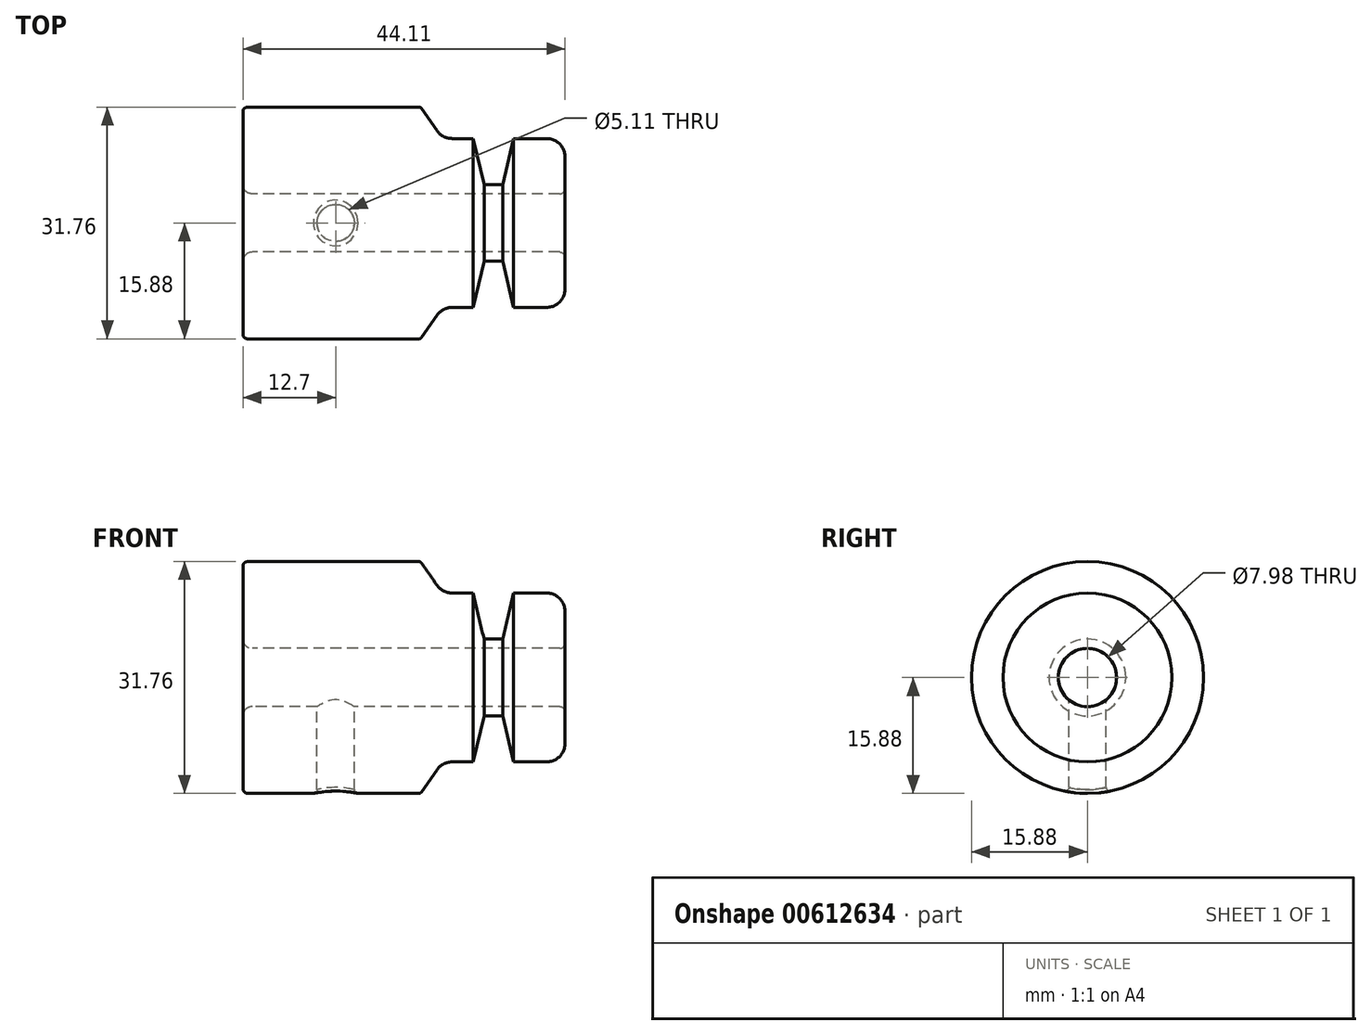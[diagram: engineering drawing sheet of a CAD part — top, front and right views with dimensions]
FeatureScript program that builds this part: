
annotation { "Feature Type Name" : "Feature", "Feature Type Description" : "" }
export const myFeature = defineFeature(function(context is Context, id is Id, definition is map)
    precondition{}
    {
        {
            var Q0;
            Q0=qCreatedBy(makeId("Top.planeOp"),FACE);
            var sketch = newSketch(context, id + "F0", { "sketchPlane" : qUnion([Q0])});
            skLineSegment(sketch, "E0", {"start": v(-39.61, 0) * mm, "end": v(40.88, 0) * mm});
            skLineSegment(sketch, "E1", {"start": v(-11.43, 3.99) * mm, "end": v(21.6, 3.99) * mm});
            skLineSegment(sketch, "E2", {"start": v(31.41, 11.27) * mm, "end": v(31.41, 11.57) * mm});
            skLineSegment(sketch, "E3", {"start": v(15.69, 15.88) * mm, "end": v(-12.07, 15.88) * mm});
            skPoint(sketch, "E4.startSnap0", {"position": v(-21.2, 9.35) * mm});
            skLineSegment(sketch, "E5", {"start": v(-12.7, 15.24) * mm, "end": v(-12.7, 5.26) * mm});
            skPoint(sketch, "E6.visualSharp", {"position": v(-12.7, 15.88) * mm});
            skArc(sketch, "E6.filletArc", {"start": v(-12.07, 15.88) * mm, "mid": v(-12.51, 15.69) * mm, "end": v(-12.7, 15.24) * mm});
            skArc(sketch, "E7.filletArc", {"start": v(-12.7, 5.26) * mm, "mid": v(-12.33, 4.36) * mm, "end": v(-11.43, 3.99) * mm});
            skPoint(sketch, "E8.visualSharp", {"position": v(31.41, 3.99) * mm});
            skPoint(sketch, "E9.visualSharp", {"position": v(31.41, 15.88) * mm});
            skPoint(sketch, "E10.visualSharp", {"position": v(23.2, 11.3) * mm});
            skPoint(sketch, "E11.visualSharp", {"position": v(19.8, -6.08) * mm});
            skPoint(sketch, "E12", {"position": v(0, 15.88) * mm});
            skPoint(sketch, "E13.visualSharp", {"position": v(25.82, 14.6) * mm});
            skPoint(sketch, "E14.visualSharp", {"position": v(17.78, 15.88) * mm});
            skLineSegment(sketch, "E15", {"start": v(21.6, 3.99) * mm, "end": v(30.67, 3.99) * mm});
            skLineSegment(sketch, "E16", {"start": v(31.41, 11.27) * mm, "end": v(31.41, 4.73) * mm});
            skLineSegment(sketch, "E17", {"start": v(31.41, 11.57) * mm, "end": v(31.41, 15.23) * mm});
            skArc(sketch, "E18.filletArc", {"start": v(30.67, 3.99) * mm, "mid": v(31.2, 4.2) * mm, "end": v(31.41, 4.73) * mm});
            skPoint(sketch, "E19.end.orphan", {"position": v(27.74, 14.69) * mm});
            skPoint(sketch, "E13.filletArc.start.orphan", {"position": v(26.12, 14.69) * mm});
            skPoint(sketch, "E20.visualSharp", {"position": v(25.4, 15.88) * mm});
            skPoint(sketch, "E21.filletArc.end.orphan", {"position": v(29.55, 15.88) * mm});
            skLineSegment(sketch, "E22", {"start": v(15.69, 15.88) * mm, "end": v(31.41, 15.88) * mm});
            skLineSegment(sketch, "E23", {"start": v(31.41, 15.88) * mm, "end": v(31.41, 15.23) * mm});
            skLineSegment(sketch, "E24", {"start": v(5.98, -3.53) * mm, "end": v(5.98, -4.45) * mm});
            skLineSegment(sketch, "E25", {"start": v(21.6, 5.26) * mm, "end": v(21.6, 15.88) * mm});
            skLineSegment(sketch, "E26", {"start": v(20.32, 5.26) * mm, "end": v(22.86, 5.26) * mm});
            skLineSegment(sketch, "E27", {"start": v(17.78, 15.88) * mm, "end": v(20.32, 5.26) * mm});
            skLineSegment(sketch, "E28", {"start": v(25.4, 15.88) * mm, "end": v(22.86, 5.26) * mm});
            skCircle(sketch, "E29", {"center": v(21.6, 11.15) * mm, "radius": 2.45 * mm});
            skLineSegment(sketch, "E30", {"start": v(24.37, 11.57) * mm, "end": v(31.41, 11.57) * mm});
            skLineSegment(sketch, "E31", {"start": v(18.81, 11.57) * mm, "end": v(14.6, 11.57) * mm});
            skLineSegment(sketch, "E32", {"start": v(14.6, 11.57) * mm, "end": v(11.64, 15.88) * mm});
            skSolve(sketch);
        }
        {
            var Q0;
            Q0=makeQuery(id+"F0.imprint","IMPRINT",FACE,{"disambiguationData":[TD([[makeQuery(id+"F0.imprint","IMPRINT",EDGE,{"derivedFrom":sQuery(id+"F0.wireOp",EDGE,"E1")}),1.0]])]});
            var Q1;
            Q1=sQuery(id+"F0.wireOp",EDGE,"E0");
            revolve(context, id + "F1", {"surfaceOperationType" : NewSurfaceOperationType.NEW, "entities" : qUnion([Q0]), "axis" : qUnion([Q1]), "revolveType" : RevolveType.FULL});
        }
        {
            var Q0;
            Q0=qCreatedBy(makeId("Top.planeOp"),FACE);
            var sketch = newSketch(context, id + "F2", { "sketchPlane" : qUnion([Q0])});
            skCircle(sketch, "E33", {"center": v(0, 0) * mm, "radius": 2.55 * mm});
            skSolve(sketch);
        }
        {
            var Q0;
            Q0 = qSketchRegion(id + "F2", true);
            extrude(context, id + "F3", {"entities" : qUnion([Q0]), "operationType" : NewBodyOperationType.REMOVE, "oppositeDirection" : true, "depth" : 25.4 * mm, "offsetDistance" : 25.4 * mm});
        }
        {
            var Q0;
            Q0=makeQuery(id+"F1.opRevolve","SWEPT_FACE",FACE,{"disambiguationData":[OSD([sQuery(id+"F0.wireOp",EDGE,"E3")])]});
            var Q1;
            Q1=makeQuery(id+"F1.opRevolve","SWEPT_EDGE",EDGE,{"disambiguationData":[OSD([sQuery(id+"F0.wireOp",EDGE,"ldVbNSM0-IPlC-SkTr-KRDH-d9lBBlJm8T0J"),sQuery(id+"F0.wireOp",EDGE,"xaKwrixG-jmVR-fOP0-37Qg-GENx1D9cPloC")])]});
            fillet(context, id + "F4", {"entities" : qUnion([Q0, Q1]), "radius" : 0.5 * mm, "tangentPropagation" : true, "allowEdgeOverflow" : false});
        }
        {
            var Q0;
            Q0=makeQuery(id+"F1.opRevolve","SWEPT_EDGE",EDGE,{"disambiguationData":[OSD([sQuery(id+"F0.wireOp",EDGE,"E2"),sQuery(id+"F0.wireOp",EDGE,"E17"),sQuery(id+"F0.wireOp",EDGE,"E30")])]});
            var Q1;
            Q1=makeQuery(id+"F1.opRevolve","SWEPT_EDGE",EDGE,{"disambiguationData":[OSD([sQuery(id+"F0.wireOp",EDGE,"E31"),sQuery(id+"F0.wireOp",EDGE,"E32")])]});
            fillet(context, id + "F5", {"entities" : qUnion([Q0, Q1]), "radius" : 2.54 * mm, "tangentPropagation" : true, "allowEdgeOverflow" : false});
        }
    });
